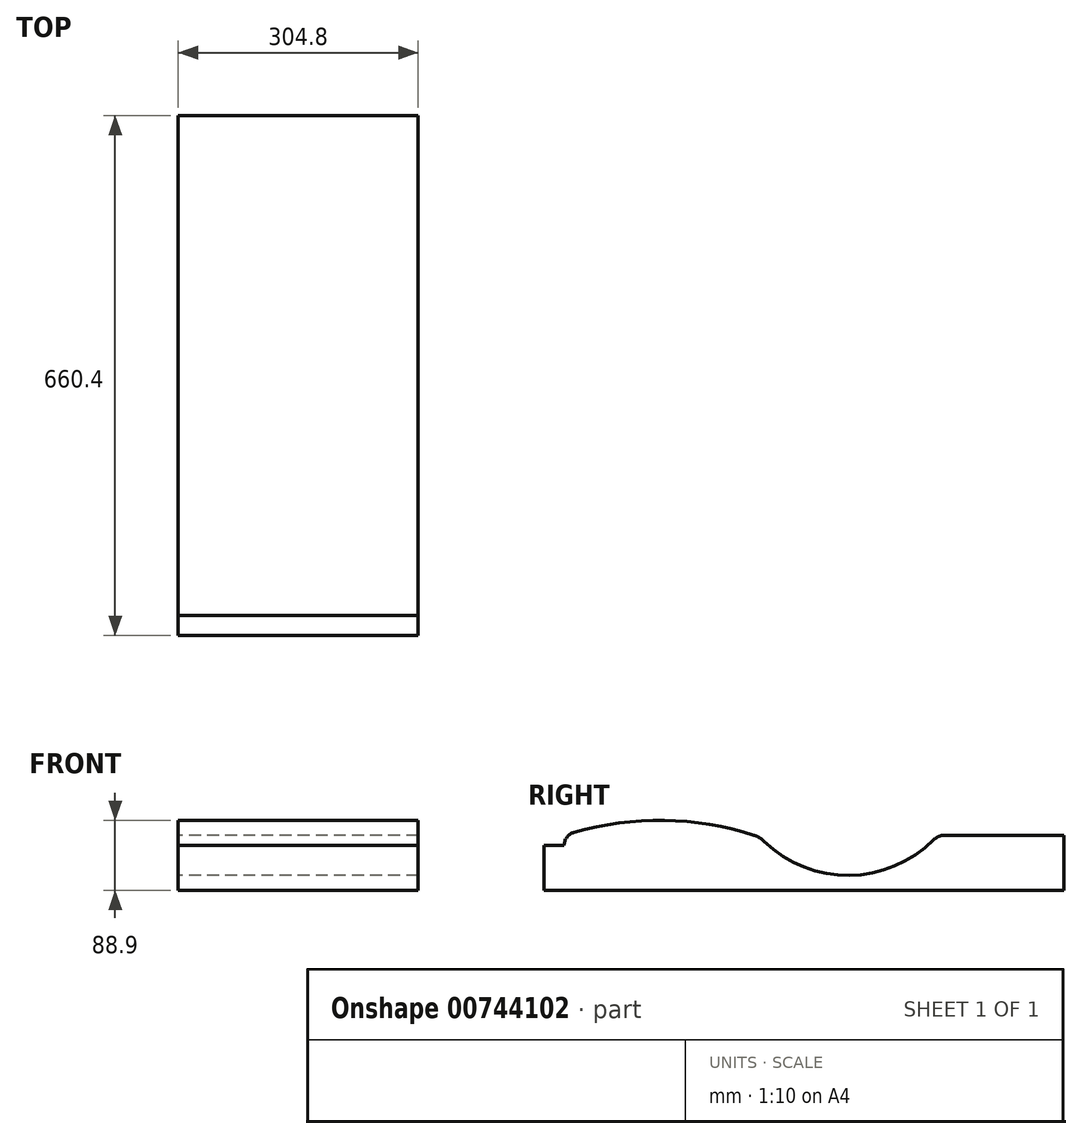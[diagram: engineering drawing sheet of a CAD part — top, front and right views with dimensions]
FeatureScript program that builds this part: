
annotation { "Feature Type Name" : "Feature", "Feature Type Description" : "" }
export const myFeature = defineFeature(function(context is Context, id is Id, definition is map)
    precondition{}
    {
        {
            var Q0;
            Q0=qCreatedBy(makeId("Right.planeOp"),FACE);
            var sketch = newSketch(context, id + "F0", { "sketchPlane" : qUnion([Q0])});
            skLineSegment(sketch, "E0", {"start": v(25.4, 0) * mm, "end": v(635, 0) * mm});
            skLineSegment(sketch, "E1", {"start": v(-26.46, 19.05) * mm, "end": v(635, 19.05) * mm, "construction": true});
            skLineSegment(sketch, "E2", {"start": v(635, 0) * mm, "end": v(635, 69.85) * mm, "construction": true});
            skLineSegment(sketch, "E3", {"start": v(266.7, 0) * mm, "end": v(266.7, 69.85) * mm, "construction": true});
            skLineSegment(sketch, "E4", {"start": v(279.4, 0) * mm, "end": v(279.4, 62.22) * mm, "construction": true});
            skLineSegment(sketch, "E5", {"start": v(508, 0) * mm, "end": v(508, 69.85) * mm, "construction": true});
            skLineSegment(sketch, "E6", {"start": v(495.3, 64.55) * mm, "end": v(495.3, 0) * mm, "construction": true});
            skArc(sketch, "E7", {"start": v(279.4, 62.22) * mm, "mid": v(387.83, 19.06) * mm, "end": v(495.3, 64.55) * mm});
            skPoint(sketch, "E8", {"position": v(386.17, 19.05) * mm});
            skLineSegment(sketch, "E9", {"start": v(635, 69.85) * mm, "end": v(508, 69.85) * mm});
            skArc(sketch, "E10", {"start": v(495.3, 64.55) * mm, "mid": v(501.12, 68.47) * mm, "end": v(508, 69.85) * mm});
            skArc(sketch, "E11", {"start": v(266.7, 69.85) * mm, "mid": v(146.05, 88.9) * mm, "end": v(25.4, 69.85) * mm, "construction": true});
            skPoint(sketch, "E12", {"position": v(146.05, 88.9) * mm});
            skArc(sketch, "E13", {"start": v(279.4, 62.22) * mm, "mid": v(273.49, 66.76) * mm, "end": v(266.7, 69.85) * mm});
            skLineSegment(sketch, "E14", {"start": v(25.4, 0) * mm, "end": v(0, 0) * mm});
            skLineSegment(sketch, "E15", {"start": v(0, 0) * mm, "end": v(0, 56.87) * mm});
            skLineSegment(sketch, "E16", {"start": v(25.4, 69.85) * mm, "end": v(25.4, 0) * mm, "construction": true});
            skLineSegment(sketch, "E17", {"start": v(635, 69.85) * mm, "end": v(660.4, 69.85) * mm});
            skLineSegment(sketch, "E18", {"start": v(660.4, 69.85) * mm, "end": v(660.4, 0) * mm});
            skLineSegment(sketch, "E19", {"start": v(660.4, 0) * mm, "end": v(635, 0) * mm});
            skArc(sketch, "E20", {"start": v(38.1, 73.73) * mm, "mid": v(28.93, 67.42) * mm, "end": v(25.4, 56.87) * mm});
            skLineSegment(sketch, "E21", {"start": v(25.4, 56.87) * mm, "end": v(0, 56.87) * mm});
            skArc(sketch, "E22", {"start": v(266.7, 69.85) * mm, "mid": v(152.69, 88.84) * mm, "end": v(38.1, 73.73) * mm});
            skLineSegment(sketch, "E23", {"start": v(38.1, 73.73) * mm, "end": v(38.1, 0) * mm, "construction": true});
            skSolve(sketch);
        }
        {
            var Q0;
            Q0 = qSketchRegion(id + "F0", true);
            extrude(context, id + "F1", {"entities" : qUnion([Q0]), "depth" : 304.8 * mm, "offsetDistance" : 25.4 * mm});
        }
    });
